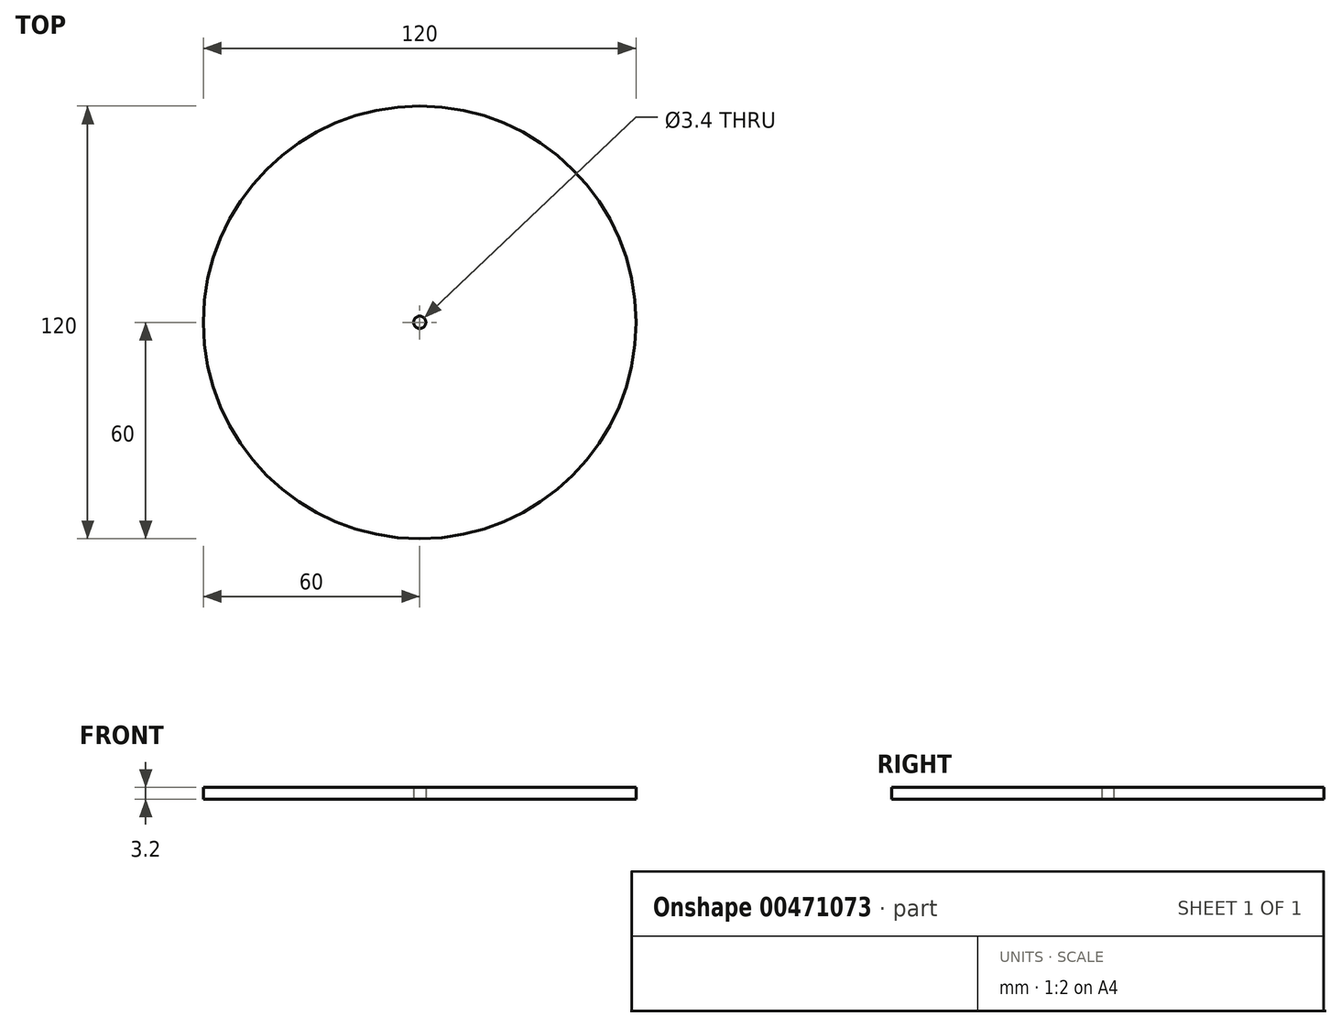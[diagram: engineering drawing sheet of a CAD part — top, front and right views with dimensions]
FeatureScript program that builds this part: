
annotation { "Feature Type Name" : "Feature", "Feature Type Description" : "" }
export const myFeature = defineFeature(function(context is Context, id is Id, definition is map)
    precondition{}
    {
        {
            var Q0;
            Q0=qCreatedBy(makeId("Top.planeOp"),FACE);
            var sketch = newSketch(context, id + "F0", { "sketchPlane" : qUnion([Q0])});
            skCircle(sketch, "E0", {"center": v(0, 0) * mm, "radius": 60 * mm});
            skCircle(sketch, "E1", {"center": v(0, 0) * mm, "radius": 1.7 * mm});
            skSolve(sketch);
        }
        {
            var Q0;
            Q0 = qSketchRegion(id + "F0", true);
            extrude(context, id + "F1", {"entities" : qUnion([Q0]), "depth" : 3.2 * mm});
        }
    });
